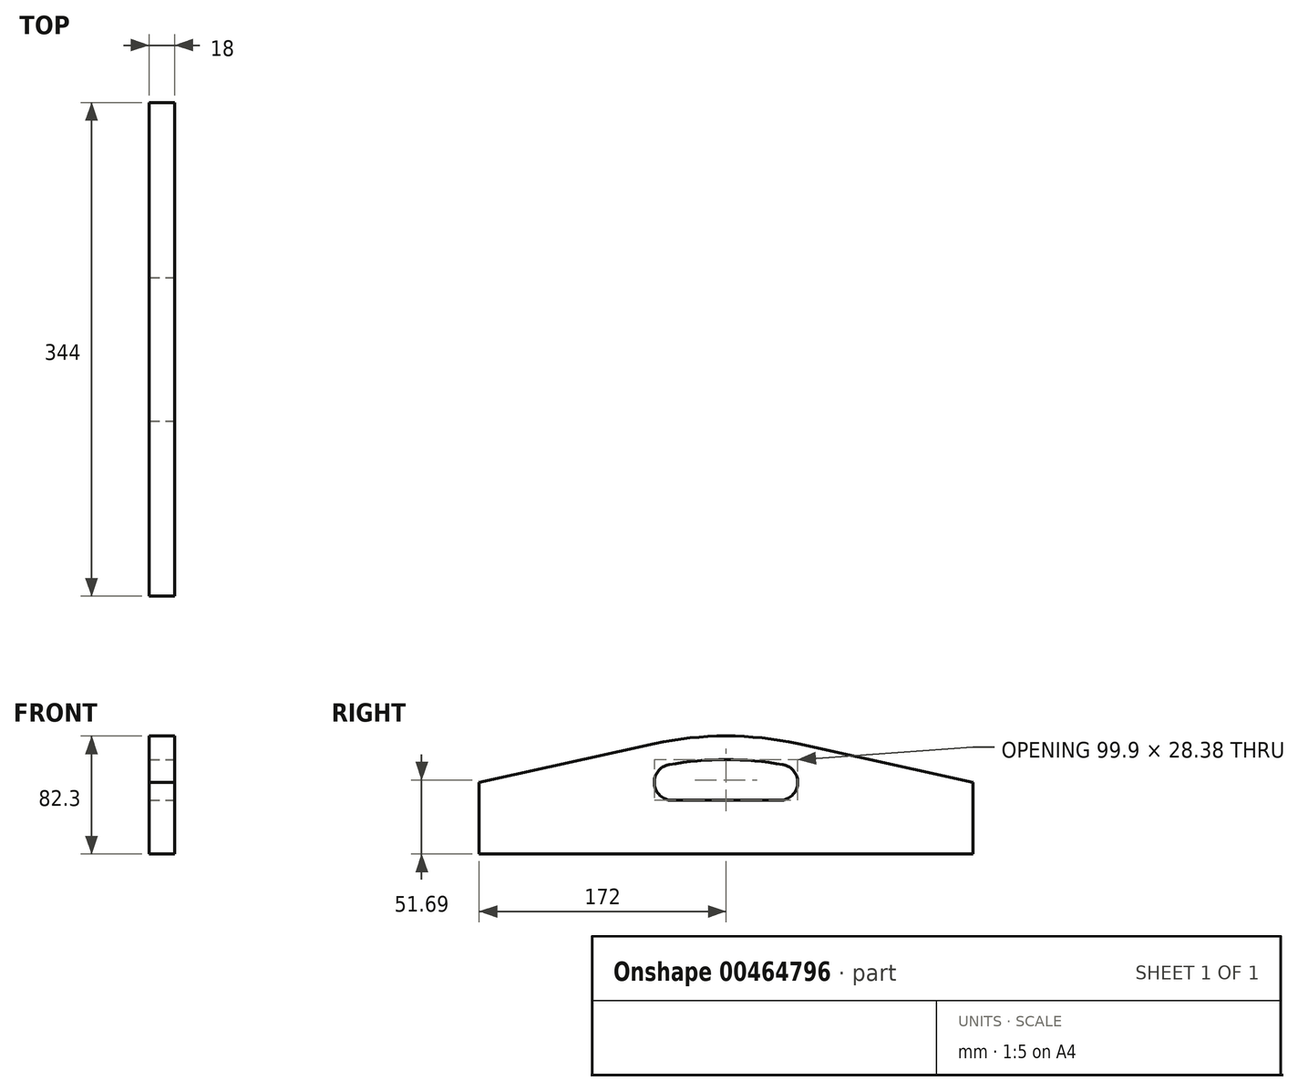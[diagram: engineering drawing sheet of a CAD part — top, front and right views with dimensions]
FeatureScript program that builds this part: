
annotation { "Feature Type Name" : "Feature", "Feature Type Description" : "" }
export const myFeature = defineFeature(function(context is Context, id is Id, definition is map)
    precondition{}
    {
        {
            var Q0;
            Q0=qCreatedBy(makeId("Right.planeOp"),FACE);
            var sketch = newSketch(context, id + "F0", { "sketchPlane" : qUnion([Q0])});
            skLineSegment(sketch, "E0.bottom", {"start": v(0, 0) * mm, "end": v(344, 0) * mm});
            skLineSegment(sketch, "E0.top", {"start": v(0, 100) * mm, "end": v(344, 100) * mm, "construction": true});
            skLineSegment(sketch, "E0.left", {"start": v(0, 0) * mm, "end": v(0, 100) * mm});
            skLineSegment(sketch, "E0.right", {"start": v(344, 0) * mm, "end": v(344, 100) * mm});
            skPoint(sketch, "E1", {"position": v(122, 100) * mm});
            skPoint(sketch, "E2", {"position": v(222, 100) * mm});
            skLineSegment(sketch, "E3", {"start": v(122, 100) * mm, "end": v(122, 0) * mm, "construction": true});
            skLineSegment(sketch, "E4", {"start": v(222, 100) * mm, "end": v(222, 0) * mm, "construction": true});
            skArc(sketch, "E5", {"start": v(122, 77) * mm, "mid": v(172, 82.3) * mm, "end": v(222, 77) * mm});
            skLineSegment(sketch, "E6", {"start": v(0, 50) * mm, "end": v(122, 77) * mm});
            skLineSegment(sketch, "E7", {"start": v(344, 50) * mm, "end": v(222, 77) * mm});
            skPoint(sketch, "E8.newPointB", {"position": v(344, 50) * mm});
            skPoint(sketch, "E9.orphan", {"position": v(0, 50) * mm});
            skSolve(sketch);
        }
        {
            var Q0;
            Q0 = qSketchRegion(id + "F0", true);
            extrude(context, id + "F1", {"entities" : qUnion([Q0]), "depth" : 18 * mm});
        }
        {
            var Q0;
            Q0=makeQuery(id+"F1.opExtrude","CAP_FACE",FACE,{"disambiguationData":[OSD([sQuery(id+"F0.wireOp",EDGE,"E0.bottom"),sQuery(id+"F0.wireOp",EDGE,"E0.left"),sQuery(id+"F0.wireOp",EDGE,"E0.right"),sQuery(id+"F0.wireOp",EDGE,"hojcP1TL-Xpnx-iaRk-RxsB-XFSz29LCahgp"),sQuery(id+"F0.wireOp",EDGE,"atJYV5Rb-Yel0-aSoY-TR2I-Oknle9Pxrf5G"),sQuery(id+"F0.wireOp",EDGE,"E5")])],"isStart":false});
            var sketch = newSketch(context, id + "F2", { "sketchPlane" : qUnion([Q0])});
            skLineSegment(sketch, "E10", {"start": v(0, 0) * mm, "end": v(344, 0) * mm, "construction": true});
            skLineSegment(sketch, "E11", {"start": v(134.5, 37.5) * mm, "end": v(209.5, 37.5) * mm});
            skArc(sketch, "E12", {"start": v(209.5, 37.5) * mm, "mid": v(218.34, 41.16) * mm, "end": v(222, 50) * mm});
            skArc(sketch, "E13", {"start": v(122, 50) * mm, "mid": v(125.66, 41.16) * mm, "end": v(134.5, 37.5) * mm});
            skLineSegment(sketch, "E14", {"start": v(0, 50) * mm, "end": v(344, 50) * mm, "construction": true});
            skLineSegment(sketch, "E15", {"start": v(134.5, 79.33) * mm, "end": v(134.5, 0) * mm, "construction": true});
            skLineSegment(sketch, "E16", {"start": v(209.5, 79.33) * mm, "end": v(209.5, 0) * mm, "construction": true});
            skLineSegment(sketch, "E17", {"start": v(172, 82.3) * mm, "end": v(172, -156.3) * mm, "construction": true});
            skLineSegment(sketch, "E18", {"start": v(172, -156.3) * mm, "end": v(113.83, 163.72) * mm, "construction": true});
            skLineSegment(sketch, "E19", {"start": v(172, -156.3) * mm, "end": v(230.07, 163.15) * mm, "construction": true});
            skPoint(sketch, "E20", {"position": v(132.26, 62.3) * mm});
            skArc(sketch, "E21", {"start": v(122, 50) * mm, "mid": v(124.9, 58) * mm, "end": v(132.26, 62.3) * mm});
            skPoint(sketch, "E22", {"position": v(211.74, 62.3) * mm});
            skArc(sketch, "E23", {"start": v(222, 50) * mm, "mid": v(219.1, 58) * mm, "end": v(211.74, 62.3) * mm});
            skArc(sketch, "E24", {"start": v(211.74, 62.3) * mm, "mid": v(172, 65.88) * mm, "end": v(132.26, 62.3) * mm});
            skSolve(sketch);
        }
        {
            var Q0;
            Q0 = qSketchRegion(id + "F2", true);
            extrude(context, id + "F3", {"entities" : qUnion([Q0]), "operationType" : NewBodyOperationType.REMOVE, "oppositeDirection" : true, "depth" : 25 * mm});
        }
    });
